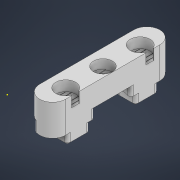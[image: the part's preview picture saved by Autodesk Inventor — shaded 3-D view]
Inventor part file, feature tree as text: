
AUTODESK INVENTOR PART (.ipt)
format: ipt  version: 2022.1 (Build 261234000, 234)  size: 371,200 bytes
history: native  units: mm
features: sketch x8, projected_geometry x6, extrude x5, fillet x5, move_body x5, direct_edit x4, hole x2, chamfer x2
ambient origin geometry x8: Origin, YZ Plane, XZ Plane, XY Plane, X Axis, Y Axis, Z Axis, Center Point
bodies: Volumenkörper1 (feature_tree)
feature tree (37):
  extrude  "Extrusion1"  Depth=10.0mm
  hole  "Bohrung1"  [1 undecoded]
  hole  "Bohrung2"  [1 undecoded]
  fillet  "Rundung1"  Radius=22.92mm
  sketch  "Skizze5"  dims[d6=3.12mm d7=6.0mm d8=5.8mm d9=3.2mm d10=90.0deg d11=8.8mm d12=0.0mm d13=11.46mm d14=22.92mm]
  extrude  "Extrusion2"  Depth=0.1mm
  direct_edit  "Direktbearbeitung1"
  direct_edit  "Direktbearbeitung2"
  fillet  "Rundung2"  Radius=12.0mm
  fillet  "Rundung3"  Radius=6.0mm
  extrude  "Extrusion3"  TaperAngle=0.0deg  [1 undecoded]
  fillet  "Rundung4"  Radius=4.0mm
  chamfer  "Fase1"  Distance=0.8mm
  direct_edit  "Direktbearbeitung3"
  fillet  "Rundung5"  Radius=6.0mm
  extrude  "Extrusion4"  Depth=7.0mm
  extrude  "Extrusion5"  Depth=6.0mm
  chamfer  "Fase2"  Distance=7.0mm
  direct_edit  "Direktbearbeitung4"
  sketch  "Skizze1"  dims[d0=10.0mm d1=45.0mm]
  sketch  "Skizze2"  dims[d2=6.8mm d3=0.0mm d4=7.0mm]
  sketch  "Skizze3"  dims[d5=0.0mm]
  sketch  "Skizze6"  dims[d15=6.1mm d16=6.0mm d17=5.8mm d18=3.2mm d19=90.0deg d20=3.6mm d21=0.0mm d22=0.1mm d26=12.0mm d27=6.0mm]
  sketch  "Skizze7"  dims[d28=1.0mm d29=0.0mm d30=0.0mm d31=0.0mm d32=-4.0mm]
  projected_geometry  "Projizierte Kontur3"
  projected_geometry  "Projizierte Kontur4"
  sketch  "Skizze8"  dims[d33=0.0mm d34=0.0mm d35=-4.0mm]
  projected_geometry  "Projizierte Kontur5"
  projected_geometry  "Projizierte Kontur6"
  projected_geometry  "Projizierte Kontur7"
  sketch  "Skizze9"  dims[d36=0.0mm d37=0.0mm d38=-2.0mm d39=4.0mm d40=0.8mm d41=6.0mm d42=7.0mm d43=6.0mm d44=7.0mm d45=7.0mm d46=7.0mm d47=5.2mm d48=0.0mm d49=1.0mm d50=0.6mm d51=2.0mm d52=45.0deg d53=0.0mm d54=0.0mm d55=2.0mm d56=1.0mm d57=3.05mm d58=6.1mm d59=2.0mm d60=0.1mm d61=1.0mm d62=0.1mm d63=2.0mm d64=0.1mm d65=1.0mm d66=0.1mm d67=0.0mm d68=0.1mm d69=0.21mm d70=0.0mm d71=0.2mm d72=0.0mm d73=0.2mm d74=2.0mm d75=45.0deg d76=0.0mm d77=0.0mm d78=-0.2mm]
  projected_geometry  "Projizierte Kontur8"
  move_body  "Verschieben1"
  move_body  "Verschieben2"
  move_body  "Verschieben3"
  move_body  "Verschieben4"
  move_body  "Verschieben5"
note: 3 required parameter values undecoded (feature->parameter linkage not recoverable at this tier; creation-order binding heuristic only, values carry confidence <= 0.55)
